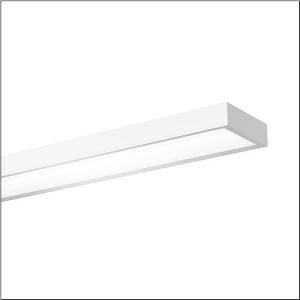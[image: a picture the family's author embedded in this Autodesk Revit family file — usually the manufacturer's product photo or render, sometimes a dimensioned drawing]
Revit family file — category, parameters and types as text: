
# Revit family: sport_31_51hs12dc4dca
name_source: partatom
category: Lighting Fixtures
units: mm (PartAtom-declared; Revit-internal decimal feet)

## family parameters
Cut with Voids When Loaded = No
Host = Face
Light Source = No
Part Type = Normal
Room Calculation Point = No
Round Connector Dimension = Use Diameter
Shared = No

## types (1)
- --- (1 x LED, 8000 lm, 59.4 W, 4000K)
    Apparent Load = 59 VA
    CIE Flux Codes = 65 89 97 100 100
    Color Rendering = 80
    Color Temperature = 4000K
    Default Elevation = 1800 mm
    Description = Sport 31, LED high bay luminaire, primary light control with reflector, of sheet steel, primary anti-glare with prismatic structure, of PC, primary optical cover: cover panel, of PC, light emission: direct distribution, primary light characteristic: symmetric, installation type: suspended mounting, recessed, surface-mounted, LED, rated luminous flux: 8.000lm, luminous efficacy: 135lm/W, light colour: 840, colour temperature: 4000K, control gear: ECG DALI, with terminal, 5-pole, max. 2.5mm², mains connection: 220..240V, AC/DC, 50/60Hz, rated input power: 58W, housing, of sheet steel, traffic white (RAL 9016), length: 1.540mm, width: 315mm, height: 95mm, protection rating (complete): IP20, protection rating (lamp compartment, on room side): IP50, insulation class (complete): insulation class I (protective earthing), certification: CE, ENEC, UKCA, ball protection: ball impact resistant with ceiling mounting or chain suspension, impact resistance: IK08, permissible operating ambient temperature: -20..+35°C, standard: DIN 18032-3, EN 60598-2-22, packaging unit: 1 piece
    Height = 100 mm  [stored 0.328084 ft]
    Lamp = 1 x LED
    Lamp Light Flux = 8000 lm
    Lamp Power = 59.4 W
    Lamp count = 1
    Length = 1500 mm
    Luminous efficacy = 135 lm/W
    Manufacturer = Siteco
    ModVariant = No
    Model = 51HS12DC4DCA
    Mounting Place = Ceiling
    Mounting Type = Pendant
    Number of Poles = 1
    OnlyDefault = Yes
    Power Factor = 1
    Product Name = Sport 31
    Product group = LED high bay luminaire
    ProductGroupID = 903
    Protection Class = Protection class I
    Protection Degree = IP 20
    RLX_Detail_Level = 1
    RLX_Emergency_Light_Flux = 0 lm
    RLX_Emergency_Type = 0
    RLX_Emergency_Type_DB = No
    RlxData = <blob elided: 22733 chars, md5=18e754ad>
    Socket = socket
    Standby Power = 0 W
    System Light Flux = 8000 lm
    System Power = 59 W
    Type Comments = factory setting: luminous flux: 100 % | dim-lin: 254 | 247 mA
    Type Image = l_1006823.jpg
    URL = http://relux.com
    VarID = @adj_151001
    Voltage = 0 V
    Weight = 0.00 kg
    Width = 315 mm

note: [stored X ft] marks values corroborated as IEEE doubles in the binary element streams (Revit-internal decimal feet)

## geometry (parser evidence)
native form markers: Blend x4, Sweep x11
no freeform markers — native parametric forms only
